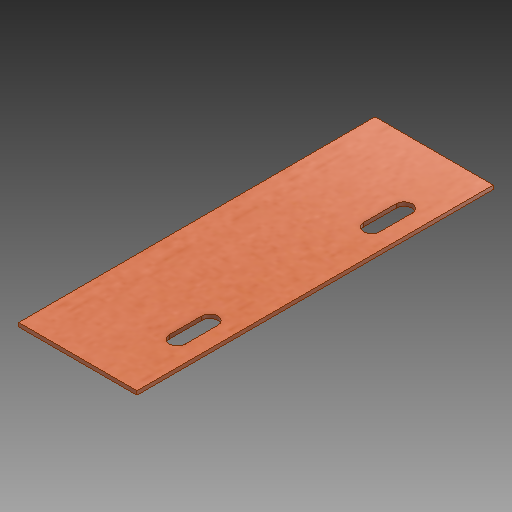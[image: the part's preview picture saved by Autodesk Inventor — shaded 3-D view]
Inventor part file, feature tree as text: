
AUTODESK INVENTOR PART (.ipt)
format: ipt  version: 2018 (Build 220112000, 112)  size: 150,528 bytes
history: native  units: mm
features: extrude x1
ambient origin geometry x8: Origin, YZ Plane, XZ Plane, XY Plane, X Axis, Y Axis, Z Axis, Center Point
bodies: Body1 (feature_tree)
feature tree (1):
  extrude  "Extrusion2"  Depth=36.5mm
